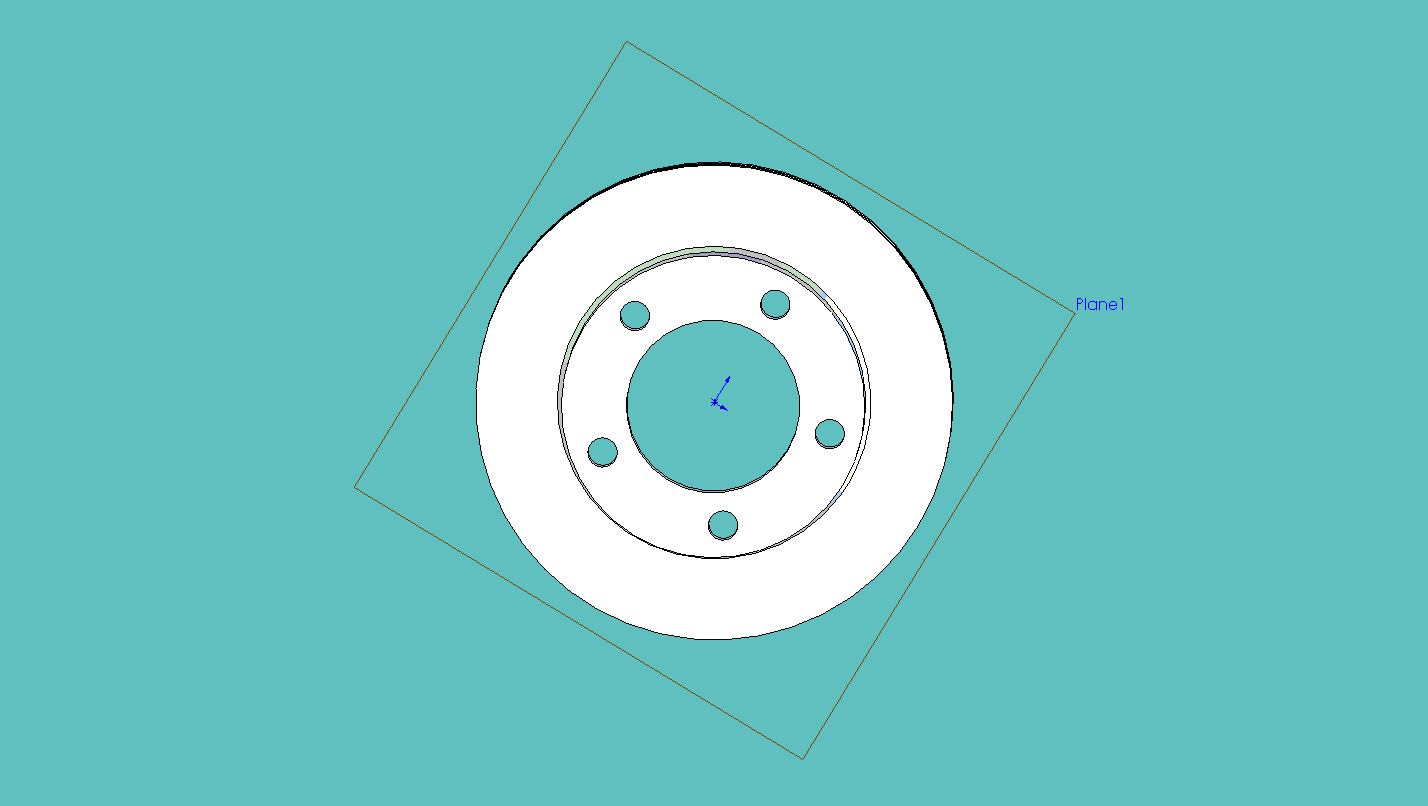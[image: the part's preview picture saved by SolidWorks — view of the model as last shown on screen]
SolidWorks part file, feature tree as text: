
SOLIDWORKS PART (.sldprt)
format: sldprt  version: not decoded by parser v0  size: 653,824 bytes
history: native  units: mm
features: sketch x5, extrude x4, material x1, chamfer x1, cut_extrude x1, plane x1 (+13 scaffold rows collapsed)
feature tree (26):
  scaffold x13  (default folders/planes/origin — collapsed)
  material  "Material <not specified>"
  sketch  "Sketch1"  dims[c1.D1=279.4mm c1.D2=177.8mm c1.D3=101.6mm c1.D4=~17.226843mm c2.D3=~94.511865mm c2.D4=~69.507869mm c2.D5=~70.192131mm]
  extrude  "Extrude4"  Depth=6.35mm
  extrude  "Extrude5"  [1 undecoded]
  sketch  "Sketch1<9>"  dims[D1=25.4mm]
  chamfer  "Chamfer1"  Distance=3mm Angle=45deg
  sketch  "Sketch2"
  cut_extrude  "Cut-Extrude1"  Depth=20mm
  sketch  "Sketch3"
  extrude  "Extrude6"  Depth=6.35mm
  plane  "Plane1"  Offset=6.35mm
  sketch  "Sketch4"
  extrude  "Extrude7"  Depth=6.35mm
decode coverage: 7 of 11 modeling features carry decoded parameters
note: ~ marks probable driven/reference dimensions
note: 1 parameter value undecoded
note: suppression state not decoded; provenance and decode notes live in map.json
